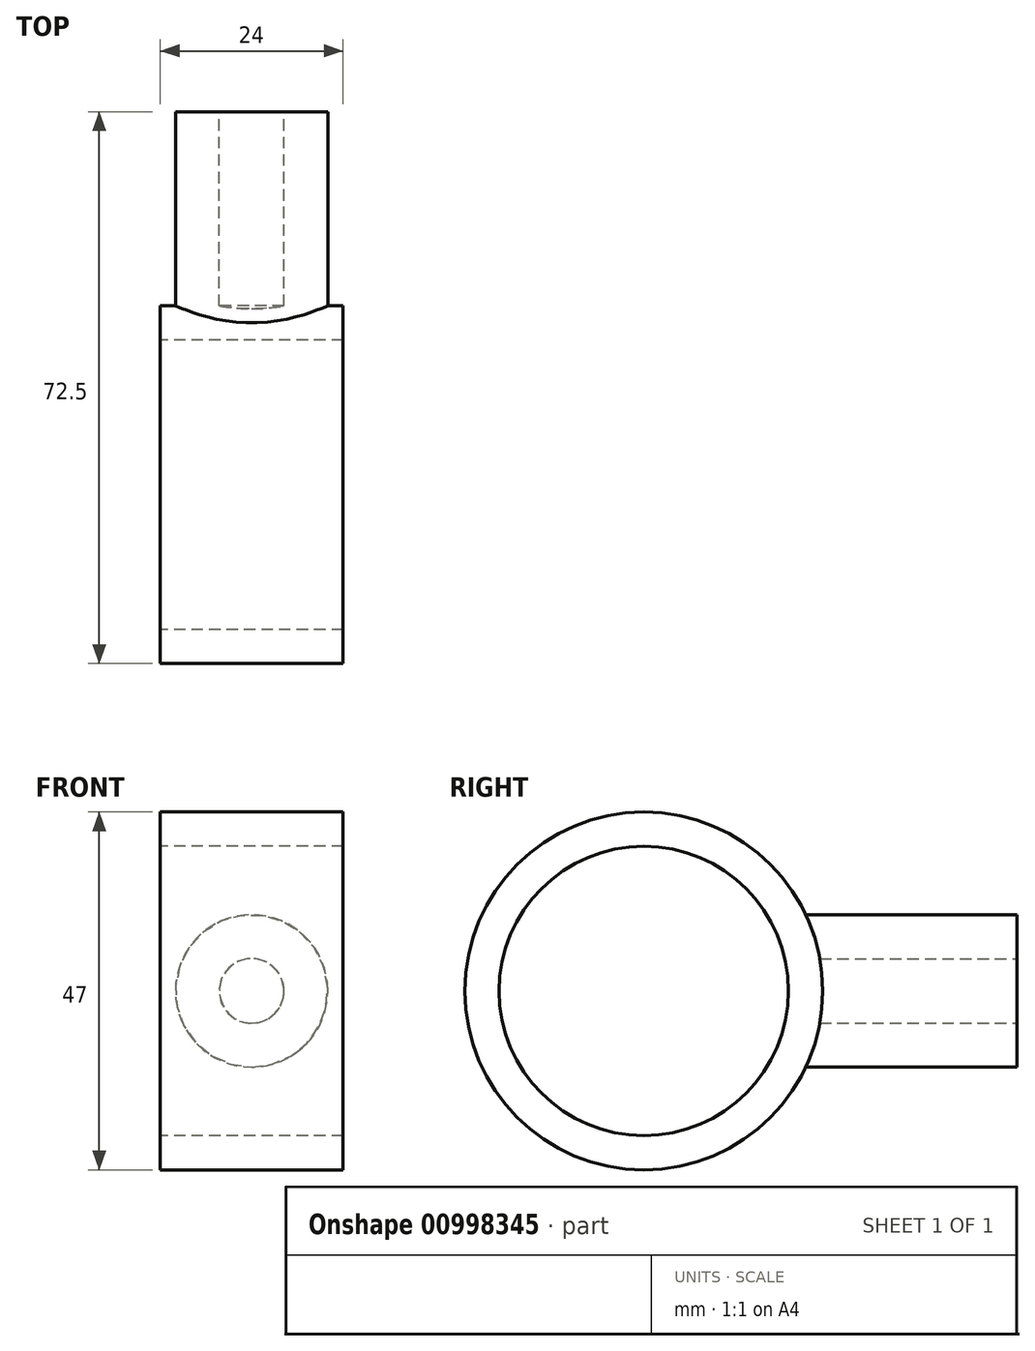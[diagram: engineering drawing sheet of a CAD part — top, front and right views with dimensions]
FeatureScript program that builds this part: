
annotation { "Feature Type Name" : "Feature", "Feature Type Description" : "" }
export const myFeature = defineFeature(function(context is Context, id is Id, definition is map)
    precondition{}
    {
        {
            var Q0;
            Q0=qCreatedBy(makeId("Front.planeOp"),FACE);
            var sketch = newSketch(context, id + "F0", { "sketchPlane" : qUnion([Q0])});
            skCircle(sketch, "E0", {"center": v(0, 0) * mm, "radius": 10 * mm});
            skCircle(sketch, "E1", {"center": v(0, 0) * mm, "radius": 4.25 * mm});
            skSolve(sketch);
        }
        {
            var Q0;
            Q0=makeQuery(id+"F0.imprint","IMPRINT",FACE,{"disambiguationData":[TD([[makeQuery(id+"F0.imprint","IMPRINT",EDGE,{"derivedFrom":sQuery(id+"F0.wireOp",EDGE,"E0")}),1.0]])]});
            extrude(context, id + "F1", {"entities" : qUnion([Q0]), "depth" : 30 * mm, "offsetDistance" : 25 * mm});
        }
        {
            var Q0;
            Q0=qCreatedBy(makeId("Right.planeOp"),FACE);
            var sketch = newSketch(context, id + "F2", { "sketchPlane" : qUnion([Q0])});
            skCircle(sketch, "E2", {"center": v(-49, 0) * mm, "radius": 19 * mm});
            skCircle(sketch, "E3", {"center": v(-49, 0) * mm, "radius": 23.5 * mm});
            skLineSegment(sketch, "E4", {"start": v(-49, 0) * mm, "end": v(0, 0) * mm, "construction": true});
            skSolve(sketch);
        }
        {
            var Q0;
            Q0=makeQuery(id+"F2.imprint","IMPRINT",FACE,{"disambiguationData":[TD([[makeQuery(id+"F2.imprint","IMPRINT",EDGE,{"derivedFrom":sQuery(id+"F2.wireOp",EDGE,"E2")}),-1.0]])]});
            extrude(context, id + "F3", {"entities" : qUnion([Q0]), "operationType" : NewBodyOperationType.ADD, "depth" : 12 * mm, "offsetDistance" : 25 * mm});
        }
        {
            var Q0;
            Q0=makeQuery(id+"F1.opExtrude","SWEPT_BODY",BODY,{"disambiguationData":[OSD([sQuery(id+"F0.wireOp",EDGE,"E0")])]});
            var Q1;
            Q1=qCreatedBy(makeId("Right.planeOp"),FACE);
            mirror(context, id + "F4", {"operationType" : NewBodyOperationType.ADD, "entities" : qUnion([Q0]), "mirrorPlane" : qUnion([Q1])});
        }
    });
